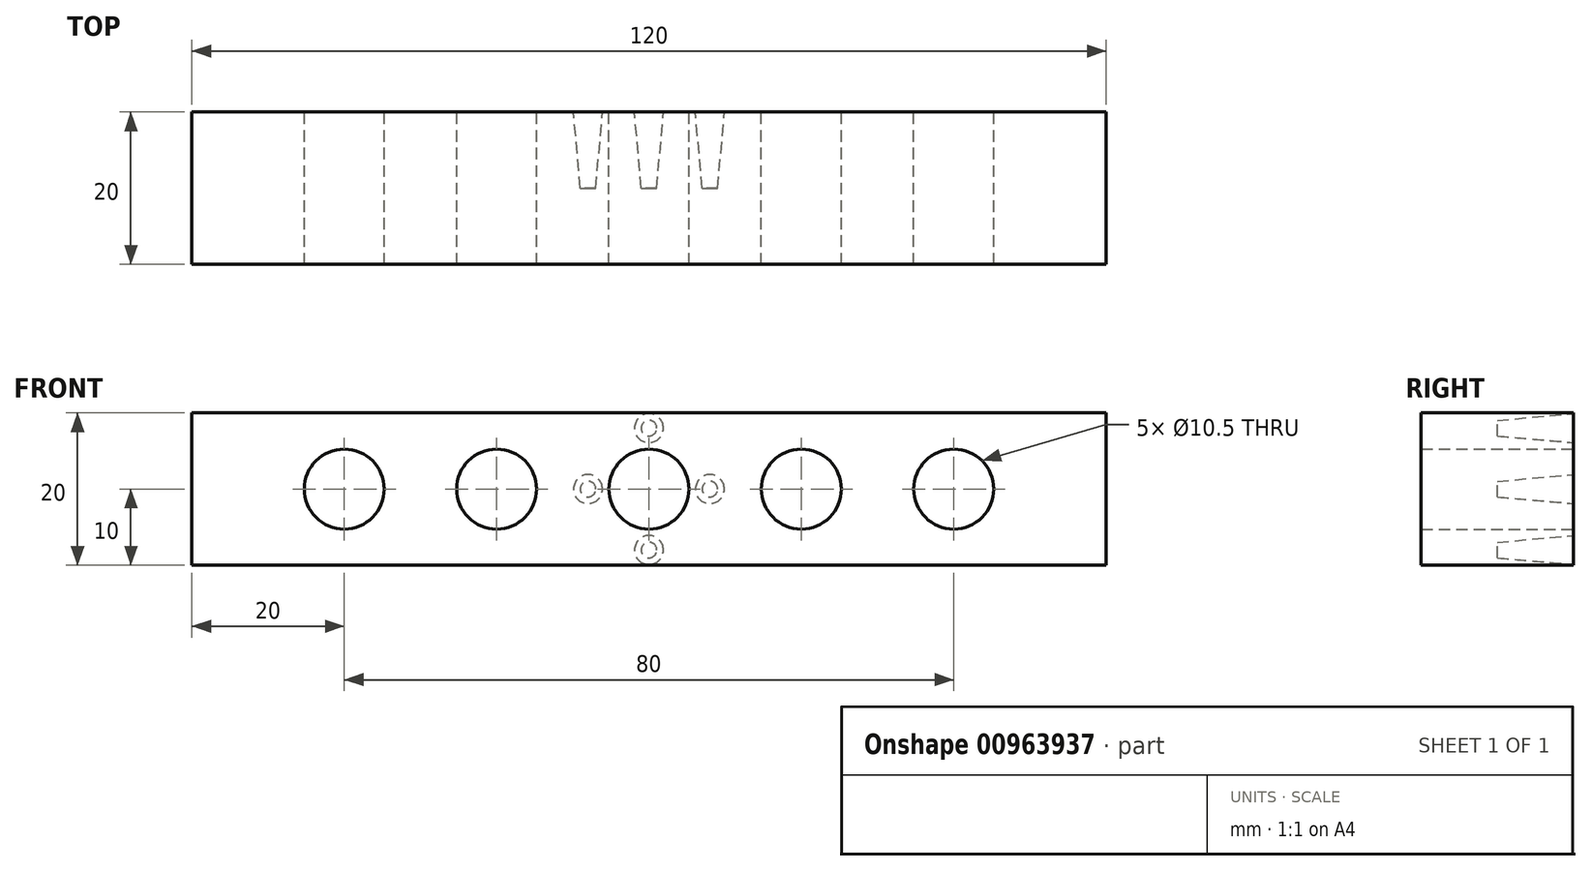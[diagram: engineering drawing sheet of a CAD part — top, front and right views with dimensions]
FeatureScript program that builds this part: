
annotation { "Feature Type Name" : "Feature", "Feature Type Description" : "" }
export const myFeature = defineFeature(function(context is Context, id is Id, definition is map)
    precondition{}
    {
        {
            var Q0;
            Q0=qCreatedBy(makeId("Front.planeOp"),FACE);
            var sketch = newSketch(context, id + "F0", { "sketchPlane" : qUnion([Q0])});
            skCircle(sketch, "E0", {"center": v(0, 10) * mm, "radius": 5.25 * mm});
            skCircle(sketch, "E1", {"center": v(-20, 10) * mm, "radius": 5.25 * mm});
            skLineSegment(sketch, "E2", {"start": v(0, 0) * mm, "end": v(0, 57.15) * mm, "construction": true});
            skCircle(sketch, "E3.MirrorC", {"center": v(20, 10) * mm, "radius": 5.25 * mm});
            skLineSegment(sketch, "E4.bottom", {"start": v(60, 0) * mm, "end": v(-60, 0) * mm});
            skLineSegment(sketch, "E4.top", {"start": v(60, 20) * mm, "end": v(-60, 20) * mm});
            skLineSegment(sketch, "E4.left", {"start": v(60, 0) * mm, "end": v(60, 20) * mm});
            skLineSegment(sketch, "E4.right", {"start": v(-60, 0) * mm, "end": v(-60, 20) * mm});
            skLineSegment(sketch, "E5", {"start": v(60, 10) * mm, "end": v(-60, 10) * mm, "construction": true});
            skCircle(sketch, "E6", {"center": v(0, 10) * mm, "radius": 8 * mm, "construction": true});
            skCircle(sketch, "E7", {"center": v(-8, 10) * mm, "radius": 1.9 * mm});
            skCircle(sketch, "E8.1.0", {"center": v(0, 2) * mm, "radius": 1.9 * mm});
            skCircle(sketch, "E8.2.0", {"center": v(8, 10) * mm, "radius": 1.9 * mm});
            skCircle(sketch, "E8.3.0", {"center": v(0, 18) * mm, "radius": 1.9 * mm});
            skCircle(sketch, "E9", {"center": v(-40, 10) * mm, "radius": 5.25 * mm});
            skCircle(sketch, "E10.MirrorC", {"center": v(40, 10) * mm, "radius": 5.25 * mm});
            skSolve(sketch);
        }
        {
            var Q0;
            Q0=makeQuery(id+"F0.imprint","IMPRINT",FACE,{"disambiguationData":[TD([[makeQuery(id+"F0.imprint","IMPRINT",EDGE,{"derivedFrom":sQuery(id+"F0.wireOp",EDGE,"E0")}),-1.0]])]});
            var Q1;
            Q1=makeQuery(id+"F0.imprint","IMPRINT",FACE,{"disambiguationData":[TD([[makeQuery(id+"F0.imprint","IMPRINT",EDGE,{"derivedFrom":sQuery(id+"F0.wireOp",EDGE,"E8.2.0")}),1.0]])]});
            var Q2;
            Q2=makeQuery(id+"F0.imprint","IMPRINT",FACE,{"disambiguationData":[TD([[makeQuery(id+"F0.imprint","IMPRINT",EDGE,{"derivedFrom":sQuery(id+"F0.wireOp",EDGE,"E8.3.0")}),1.0]])]});
            var Q3;
            Q3=makeQuery(id+"F0.imprint","IMPRINT",FACE,{"disambiguationData":[TD([[makeQuery(id+"F0.imprint","IMPRINT",EDGE,{"derivedFrom":sQuery(id+"F0.wireOp",EDGE,"E7")}),1.0]])]});
            var Q4;
            Q4=makeQuery(id+"F0.imprint","IMPRINT",FACE,{"disambiguationData":[TD([[makeQuery(id+"F0.imprint","IMPRINT",EDGE,{"derivedFrom":sQuery(id+"F0.wireOp",EDGE,"E8.1.0")}),1.0]])]});
            extrude(context, id + "F1", {"entities" : qUnion([Q0, Q1, Q2, Q3, Q4]), "depth" : 20 * mm, "offsetDistance" : 25 * mm});
        }
        {
            var Q0;
            Q0=makeQuery(id+"F0.imprint","IMPRINT",FACE,{"disambiguationData":[TD([[makeQuery(id+"F0.imprint","IMPRINT",EDGE,{"derivedFrom":sQuery(id+"F0.wireOp",EDGE,"E8.2.0")}),1.0]])]});
            var Q1;
            Q1=makeQuery(id+"F0.imprint","IMPRINT",FACE,{"disambiguationData":[TD([[makeQuery(id+"F0.imprint","IMPRINT",EDGE,{"derivedFrom":sQuery(id+"F0.wireOp",EDGE,"E8.3.0")}),1.0]])]});
            var Q2;
            Q2=makeQuery(id+"F0.imprint","IMPRINT",FACE,{"disambiguationData":[TD([[makeQuery(id+"F0.imprint","IMPRINT",EDGE,{"derivedFrom":sQuery(id+"F0.wireOp",EDGE,"E7")}),1.0]])]});
            var Q3;
            Q3=makeQuery(id+"F0.imprint","IMPRINT",FACE,{"disambiguationData":[TD([[makeQuery(id+"F0.imprint","IMPRINT",EDGE,{"derivedFrom":sQuery(id+"F0.wireOp",EDGE,"E8.1.0")}),1.0]])]});
            extrude(context, id + "F2", {"entities" : qUnion([Q0, Q1, Q2, Q3]), "operationType" : NewBodyOperationType.REMOVE, "depth" : 10 * mm, "offsetDistance" : 25 * mm, "hasDraft" : true, "draftAngle" : 5 * degree, "draftPullDirection" : true});
        }
    });
